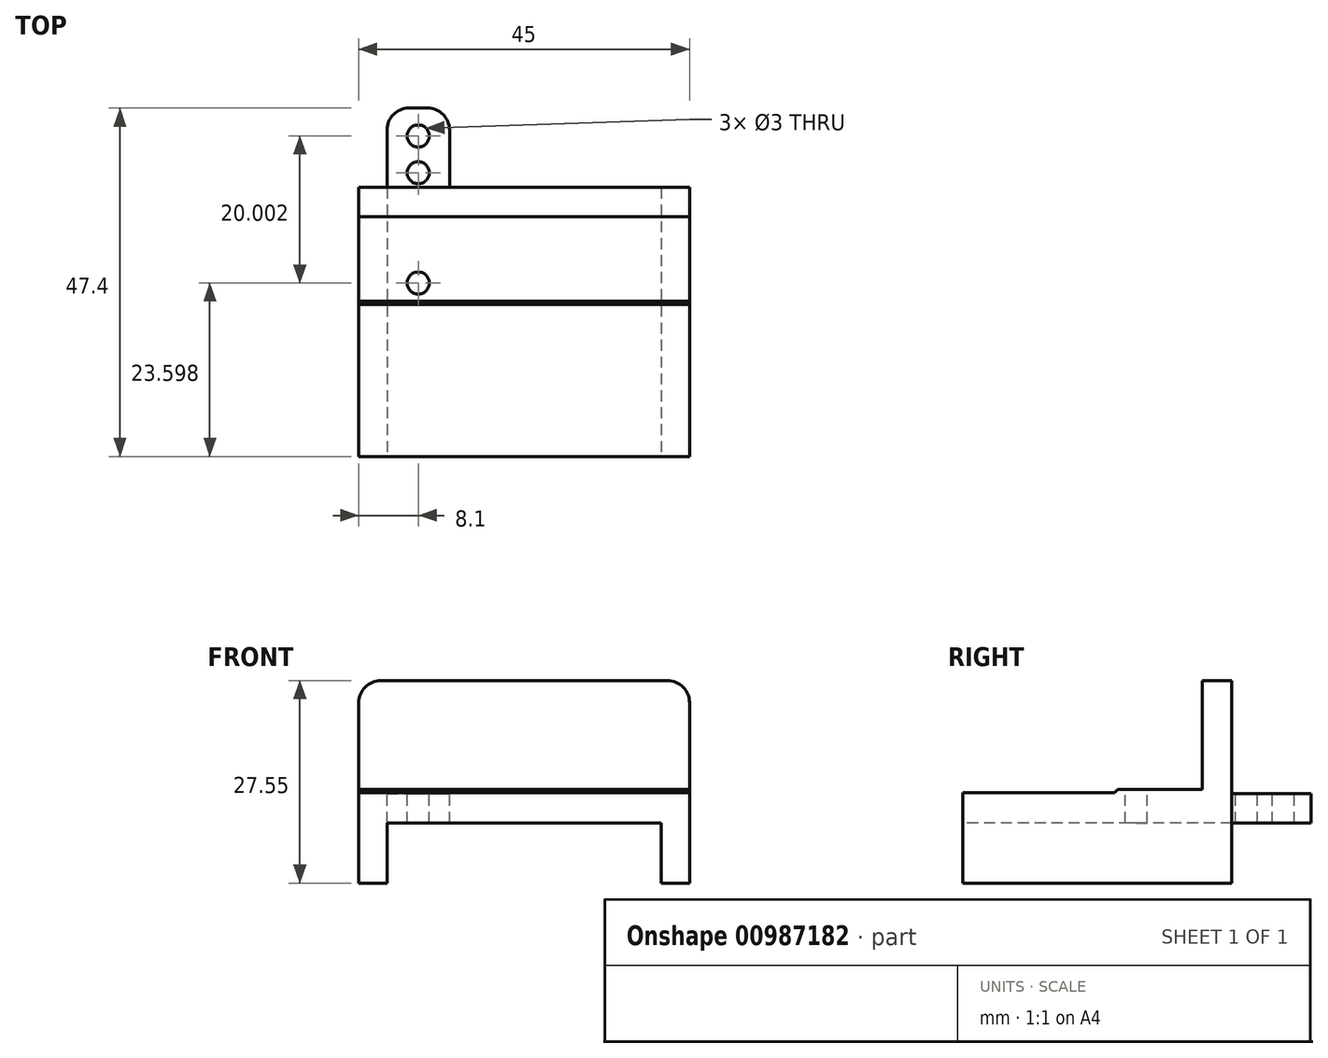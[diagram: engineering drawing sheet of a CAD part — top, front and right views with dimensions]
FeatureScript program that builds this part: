
annotation { "Feature Type Name" : "Feature", "Feature Type Description" : "" }
export const myFeature = defineFeature(function(context is Context, id is Id, definition is map)
    precondition{}
    {
        {
            var Q0;
            Q0=qCreatedBy(makeId("Top.planeOp"),FACE);
            var sketch = newSketch(context, id + "F0", { "sketchPlane" : qUnion([Q0])});
            skLineSegment(sketch, "E0.bottom", {"start": v(22.5, -18.3) * mm, "end": v(-22.5, -18.3) * mm});
            skLineSegment(sketch, "E0.top", {"start": v(22.5, 18.3) * mm, "end": v(-22.5, 18.3) * mm});
            skLineSegment(sketch, "E0.left", {"start": v(22.5, -18.3) * mm, "end": v(22.5, 18.3) * mm});
            skLineSegment(sketch, "E0.right", {"start": v(-22.5, -18.3) * mm, "end": v(-22.5, 18.3) * mm});
            skPoint(sketch, "E0.middle", {"position": v(0, 0) * mm});
            skSolve(sketch);
        }
        {
            var Q0;
            Q0 = qSketchRegion(id + "F0", true);
            extrude(context, id + "F1", {"entities" : qUnion([Q0]), "depth" : 12.3 * mm, "offsetDistance" : 25 * mm});
        }
        {
            var Q0;
            Q0=makeQuery(id+"F1.opExtrude","SWEPT_FACE",FACE,{"disambiguationData":[OSD([sQuery(id+"F0.wireOp",EDGE,"E0.bottom")])]});
            var sketch = newSketch(context, id + "F2", { "sketchPlane" : qUnion([Q0])});
            skLineSegment(sketch, "E1.bottom", {"start": v(-18.65, 0) * mm, "end": v(18.65, 0) * mm});
            skLineSegment(sketch, "E1.top", {"start": v(-18.65, 8.2) * mm, "end": v(18.65, 8.2) * mm});
            skLineSegment(sketch, "E1.left", {"start": v(-18.65, 0) * mm, "end": v(-18.65, 8.2) * mm});
            skLineSegment(sketch, "E1.right", {"start": v(18.65, 0) * mm, "end": v(18.65, 8.2) * mm});
            skSolve(sketch);
        }
        {
            var Q0;
            Q0 = qSketchRegion(id + "F2", true);
            extrude(context, id + "F3", {"entities" : qUnion([Q0]), "operationType" : NewBodyOperationType.REMOVE, "endBound" : BoundingType.THROUGH_ALL, "oppositeDirection" : true, "depth" : 25 * mm, "offsetDistance" : 25 * mm});
        }
        {
            var Q0;
            Q0=makeQuery(id+"F1.opExtrude","CAP_FACE",FACE,{"disambiguationData":[OSD([sQuery(id+"F0.wireOp",EDGE,"E0.bottom"),sQuery(id+"F0.wireOp",EDGE,"E0.top"),sQuery(id+"F0.wireOp",EDGE,"E0.left"),sQuery(id+"F0.wireOp",EDGE,"E0.right")])],"isStart":false});
            var sketch = newSketch(context, id + "F4", { "sketchPlane" : qUnion([Q0])});
            skLineSegment(sketch, "E2.bottom", {"start": v(-22.5, 18.3) * mm, "end": v(22.5, 18.3) * mm});
            skLineSegment(sketch, "E2.top", {"start": v(-22.5, 2.3) * mm, "end": v(22.5, 2.3) * mm});
            skLineSegment(sketch, "E2.left", {"start": v(-22.5, 18.3) * mm, "end": v(-22.5, 2.3) * mm});
            skLineSegment(sketch, "E2.right", {"start": v(22.5, 18.3) * mm, "end": v(22.5, 2.3) * mm});
            skSolve(sketch);
        }
        {
            var Q0;
            Q0 = qSketchRegion(id + "F4", true);
            extrude(context, id + "F5", {"entities" : qUnion([Q0]), "operationType" : NewBodyOperationType.ADD, "depth" : 0.45 * mm, "offsetDistance" : 25 * mm});
        }
        {
            var Q0;
            Q0=makeQuery(id+"F5.opExtrude","CAP_EDGE",EDGE,{"disambiguationData":[OSD([sQuery(id+"F4.wireOp",EDGE,"E2.top")])],"isStart":false});
            chamfer(context, id + "F6", {"entities" : qUnion([Q0]), "width" : .5 * mm, "tangentPropagation" : true});
        }
        {
            var Q0;
            Q0=makeQuery(id+"F5.opExtrude","CAP_FACE",FACE,{"disambiguationData":[OSD([sQuery(id+"F4.wireOp",EDGE,"E2.bottom"),sQuery(id+"F4.wireOp",EDGE,"E2.top"),sQuery(id+"F4.wireOp",EDGE,"E2.left"),sQuery(id+"F4.wireOp",EDGE,"E2.right")])],"isStart":false});
            var sketch = newSketch(context, id + "F7", { "sketchPlane" : qUnion([Q0])});
            skLineSegment(sketch, "E3.bottom", {"start": v(-22.5, 18.3) * mm, "end": v(22.5, 18.3) * mm});
            skLineSegment(sketch, "E3.top", {"start": v(-22.5, 14.3) * mm, "end": v(22.5, 14.3) * mm});
            skLineSegment(sketch, "E3.left", {"start": v(-22.5, 18.3) * mm, "end": v(-22.5, 14.3) * mm});
            skLineSegment(sketch, "E3.right", {"start": v(22.5, 18.3) * mm, "end": v(22.5, 14.3) * mm});
            skSolve(sketch);
        }
        {
            var Q0;
            Q0 = qSketchRegion(id + "F7", true);
            extrude(context, id + "F8", {"entities" : qUnion([Q0]), "operationType" : NewBodyOperationType.ADD, "depth" : 14.8 * mm, "offsetDistance" : 25 * mm});
        }
        {
            var Q0;
            Q0=makeQuery(id+"F8.opExtrude","CAP_EDGE",EDGE,{"disambiguationData":[OSD([sQuery(id+"F7.wireOp",EDGE,"E3.left")])],"isStart":false});
            var Q1;
            Q1=makeQuery(id+"F8.opExtrude","CAP_EDGE",EDGE,{"disambiguationData":[OSD([sQuery(id+"F7.wireOp",EDGE,"E3.right")])],"isStart":false});
            fillet(context, id + "F9", {"entities" : qUnion([Q0, Q1]), "radius" : 3 * mm, "tangentPropagation" : true, "allowEdgeOverflow" : false});
        }
        {
            var Q0;
            Q0=makeQuery(id+"F8.boolean.opBoolean","MERGE",FACE,{"derivedFrom":[makeQuery(id+"F5.boolean.opBoolean","MERGE",FACE,{"derivedFrom":[makeQuery(id+"F1.opExtrude","SWEPT_FACE",FACE,{"disambiguationData":[OSD([sQuery(id+"F0.wireOp",EDGE,"E0.top")])]}),makeQuery(id+"F5.opExtrude","SWEPT_FACE",FACE,{"disambiguationData":[OSD([sQuery(id+"F4.wireOp",EDGE,"E2.bottom")])]})]}),makeQuery(id+"F8.opExtrude","SWEPT_FACE",FACE,{"disambiguationData":[OSD([sQuery(id+"F7.wireOp",EDGE,"E3.bottom")])]})]});
            var sketch = newSketch(context, id + "F10", { "sketchPlane" : qUnion([Q0])});
            skLineSegment(sketch, "E4.bottom", {"start": v(18.65, 8.2) * mm, "end": v(10.15, 8.2) * mm});
            skLineSegment(sketch, "E4.top", {"start": v(18.65, 12.2) * mm, "end": v(10.15, 12.2) * mm});
            skLineSegment(sketch, "E4.left", {"start": v(18.65, 8.2) * mm, "end": v(18.65, 12.2) * mm});
            skLineSegment(sketch, "E4.right", {"start": v(10.15, 8.2) * mm, "end": v(10.15, 12.2) * mm});
            skSolve(sketch);
        }
        {
            var Q0;
            Q0 = qSketchRegion(id + "F10", true);
            extrude(context, id + "F11", {"entities" : qUnion([Q0]), "operationType" : NewBodyOperationType.ADD, "depth" : 10.8 * mm, "offsetDistance" : 25 * mm});
        }
        {
            var Q0;
            Q0=makeQuery(id+"F11.opExtrude","CAP_EDGE",EDGE,{"disambiguationData":[OSD([sQuery(id+"F10.wireOp",EDGE,"E4.right")])],"isStart":false});
            var Q1;
            Q1=makeQuery(id+"F11.opExtrude","CAP_EDGE",EDGE,{"disambiguationData":[OSD([sQuery(id+"F10.wireOp",EDGE,"E4.left")])],"isStart":false});
            fillet(context, id + "F12", {"entities" : qUnion([Q0, Q1]), "radius" : 3 * mm, "tangentPropagation" : true, "allowEdgeOverflow" : false});
        }
        {
            var Q0;
            Q0=makeQuery(id+"F11.opExtrude","SWEPT_FACE",FACE,{"disambiguationData":[OSD([sQuery(id+"F10.wireOp",EDGE,"E4.top")])]});
            var sketch = newSketch(context, id + "F13", { "sketchPlane" : qUnion([Q0])});
            skCircle(sketch, "E5", {"center": v(-14.4, 25.3) * mm, "radius": 1.5 * mm});
            skPoint(sketch, "E5.centerSnap0", {"position": v(-14.4, 29.1) * mm});
            skCircle(sketch, "E6", {"center": v(-14.4, 20.3) * mm, "radius": 1.5 * mm});
            skSolve(sketch);
        }
        {
            var Q0;
            Q0 = qSketchRegion(id + "F13", true);
            extrude(context, id + "F14", {"entities" : qUnion([Q0]), "operationType" : NewBodyOperationType.REMOVE, "oppositeDirection" : true, "depth" : 25 * mm, "offsetDistance" : 25 * mm});
        }
        {
            var Q0;
            Q0=makeQuery(id+"F5.opExtrude","CAP_FACE",FACE,{"disambiguationData":[OSD([sQuery(id+"F4.wireOp",EDGE,"E2.bottom"),sQuery(id+"F4.wireOp",EDGE,"E2.top"),sQuery(id+"F4.wireOp",EDGE,"E2.left"),sQuery(id+"F4.wireOp",EDGE,"E2.right")])],"isStart":false});
            var sketch = newSketch(context, id + "F15", { "sketchPlane" : qUnion([Q0])});
            skCircle(sketch, "E7", {"center": v(-14.4, 5.3) * mm, "radius": 1.5 * mm});
            skSolve(sketch);
        }
        {
            var Q0;
            Q0 = qSketchRegion(id + "F15", true);
            extrude(context, id + "F16", {"entities" : qUnion([Q0]), "operationType" : NewBodyOperationType.REMOVE, "oppositeDirection" : true, "depth" : 25 * mm, "offsetDistance" : 25 * mm});
        }
    });
